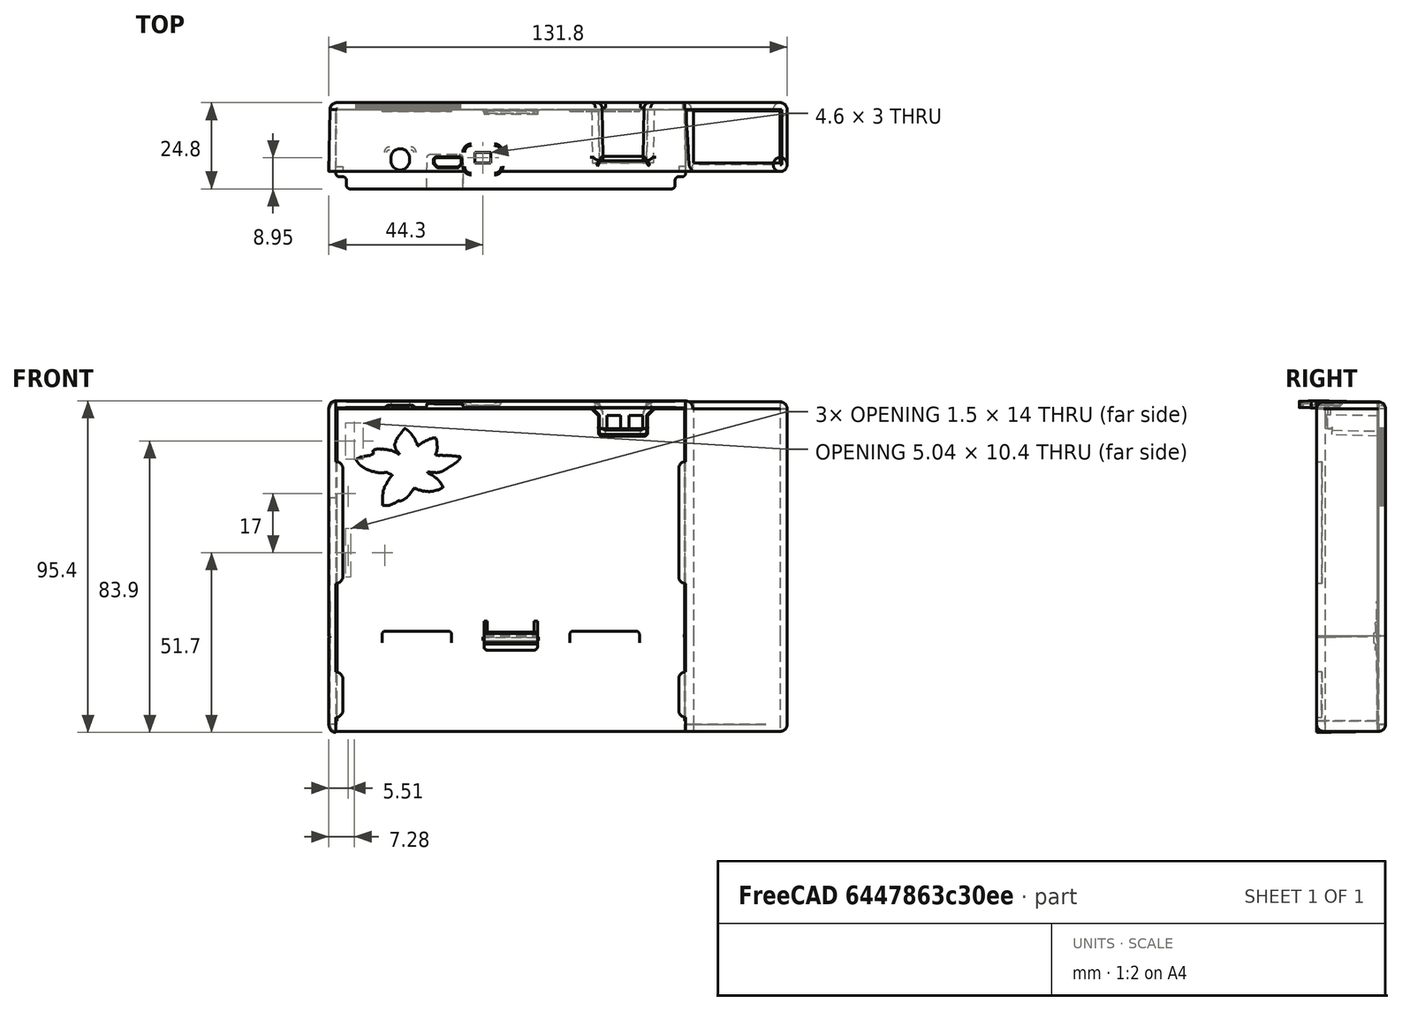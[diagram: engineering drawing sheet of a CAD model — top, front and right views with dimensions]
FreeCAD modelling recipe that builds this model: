
FCSTD DOCUMENT  (FreeCAD 0.20R29410 (Git))
Label: N2CaseOnePeice_10_18_2022
License: All rights reserved
LicenseURL: http://en.wikipedia.org/wiki/All_rights_reserved
objects: Part::Box×22, Part::Cylinder×12, Part::MultiFuse×9, Part::Cut×9, Part::Sphere×4, Part::Feature×3, Mesh::Feature×1
note: 59 computed .brp shape members not serialized (recipe doc carries the construction recipe); baked Part::Feature solids carry a one-line shape summary decoded from their .brp

FEATURE [Part::Feature] Solid  label="N2_BOTTOM_COVER"
  shape: bbox 104.6 x 25.21 x 71.78 mm, 343 faces (baked)
FEATURE [Part::Feature] Solid001  label="N2_TOP_COVER"
  shape: bbox 104.6 x 24.81 x 29.22 mm, 349 faces (baked)
FEATURE [Part::Box] Box  label="Cube"
  AttacherType = Attacher::AttachEngine3D
  Height = 15
  Length = 62.5
  Placement = pos=(-49,18,44) rot=(0,1,0;1.5708rad)
  Width = 2
FEATURE [Part::MultiFuse] Fusion  label="BottomCover"
  Shapes = -> [Solid,Box]
FEATURE [Part::Box] Box001  label="Cube001"
  AttacherType = Attacher::AttachEngine3D
  Height = 15
  Length = 97.5
  Placement = pos=(48.5,20,-3.5) rot=(0,1,0;3.14159rad)
  Width = 2
FEATURE [Part::Cut] Cut
  Base = -> Fusion
  Tool = -> Box001
FEATURE [Part::Box] Box002  label="usbEthernet"
  AttacherType = Attacher::AttachEngine3D
  Height = 25
  Length = 72
  Placement = pos=(52.5,2.6,47.4) rot=(0,1,0;1.5708rad)
  Width = 15
FEATURE [Part::Box] Box003  label="usbEthernetCover"
  AttacherType = Attacher::AttachEngine3D
  Height = 27.5
  Length = 72
  Placement = pos=(50.5,2.2,47.4) rot=(0,1,0;1.5708rad)
  Width = 15.85
FEATURE [Part::Box] Box004  label="usbEthernetCover001"
  AttacherType = Attacher::AttachEngine3D
  Height = 27.52
  Length = 65.19
  Placement = pos=(49.98,17.6,45.39) rot=(0,1,0;1.5708rad)
  Width = 2.4
FEATURE [Part::Box] Box005  label="usbEthernetCover002"
  AttacherType = Attacher::AttachEngine3D
  Height = 2
  Length = 65.19
  Placement = pos=(77.5,2.2,45.39) rot=(0,1,0;1.5708rad)
  Width = 15.8
FEATURE [Part::Cylinder] Cylinder
  Angle = 90
  AttacherType = Attacher::AttachEngine3D
  FirstAngle = 0
  Height = 65.2
  Placement = pos=(77.5,2.2,-19.8) rot=(0,0,-1;1.5708rad)
  Radius = 2
  SecondAngle = 0
FEATURE [Part::Cylinder] Cylinder001
  Angle = 90
  AttacherType = Attacher::AttachEngine3D
  FirstAngle = 0
  Height = 27.5
  Placement = pos=(77.5,18,45.4) rot=(0,-1,0;1.5708rad)
  Radius = 2
  SecondAngle = 0
FEATURE [Part::Cylinder] Cylinder002
  Angle = 90
  AttacherType = Attacher::AttachEngine3D
  FirstAngle = 0
  Height = 15.8
  Placement = pos=(77.5,2.2,45.4) rot=(0.57735,0.57735,0.57735;4.18879rad)
  Radius = 2
  SecondAngle = 0
FEATURE [Part::Cylinder] Cylinder003
  Angle = 90
  AttacherType = Attacher::AttachEngine3D
  FirstAngle = 0
  Height = 65.2
  Placement = pos=(77.5,18,-19.8) rot=(0,0,1;0rad)
  Radius = 2
  SecondAngle = 0
FEATURE [Part::Box] Box006  label="usbEthernetCover003"
  AttacherType = Attacher::AttachEngine3D
  Height = 27.2
  Length = 65.19
  Placement = pos=(50.3,0.2,45.39) rot=(0,1,0;1.5708rad)
  Width = 2.4
FEATURE [Part::Cylinder] Cylinder004
  Angle = 90
  AttacherType = Attacher::AttachEngine3D
  FirstAngle = 0
  Height = 26.4
  Placement = pos=(77.5,2.2,45.4) rot=(0.57735,-0.57735,-0.57735;2.0944rad)
  Radius = 2
  SecondAngle = 0
FEATURE [Part::Sphere] Sphere
  Angle1 = -90
  Angle2 = 90
  Angle3 = 360
  AttacherType = Attacher::AttachEngine3D
  Placement = pos=(77.5,18,45.4) rot=(0,0,1;0rad)
  Radius = 2
FEATURE [Part::Sphere] Sphere001
  Angle1 = -90
  Angle2 = 90
  Angle3 = 360
  AttacherType = Attacher::AttachEngine3D
  Placement = pos=(77.5,2.2,45.4) rot=(0,0,1;0rad)
  Radius = 2
FEATURE [Part::MultiFuse] Fusion001  label="usbCover"
  Shapes = -> [Box003,Box004,Box005,Cylinder,Cylinder001,Cylinder002,Cylinder003,Box006,Cylinder004,Sphere,Sphere001]
FEATURE [Part::MultiFuse] Fusion002
  Shapes = -> [Cut,Fusion001]
FEATURE [Part::Cut] Cut001  label="front"
  Base = -> Fusion002
  Tool = -> Box002
FEATURE [Part::Box] Box007  label="Cube002"
  AttacherType = Attacher::AttachEngine3D
  Height = 10
  Length = 30
  Placement = pos=(79.5,0,-19.8) rot=(0,1,0;3.14159rad)
  Width = 20
FEATURE [Part::Cut] Cut002
  Base = -> Cut001
  Tool = -> Box007
FEATURE [Part::Box] Box008  label="Cube003"
  AttacherType = Attacher::AttachEngine3D
  Height = 10
  Length = 30
  Placement = pos=(79.5,0,-19.8) rot=(0,1,0;3.14159rad)
  Width = 20
FEATURE [Part::Cut] Cut003  label="front001"
  Base = -> Cut002
  Tool = -> Box008
FEATURE [Part::Box] Box009  label="usbEthernet001"
  AttacherType = Attacher::AttachEngine3D
  Height = 25
  Length = 72
  Placement = pos=(52.5,2.6,6.3) rot=(0,1,0;1.5708rad)
  Width = 15
FEATURE [Part::Box] Box010  label="usbEthernetCover004"
  AttacherType = Attacher::AttachEngine3D
  Height = 27.5
  Length = 72
  Placement = pos=(50.5,2.2,-19.8) rot=(0,1,0;1.5708rad)
  Width = 15.85
FEATURE [Part::Box] Box011  label="usbEthernetCover005"
  AttacherType = Attacher::AttachEngine3D
  Height = 27.52
  Length = 65.19
  Placement = pos=(49.98,17.6,-19.8) rot=(0,1,0;1.5708rad)
  Width = 2.4
FEATURE [Part::Box] Box012  label="usbEthernetCover006"
  AttacherType = Attacher::AttachEngine3D
  Height = 2
  Length = 65.19
  Placement = pos=(77.5,2.2,-19.8) rot=(0,1,0;1.5708rad)
  Width = 15.8
FEATURE [Part::Box] Box013  label="usbEthernetCover007"
  AttacherType = Attacher::AttachEngine3D
  Height = 27.2
  Length = 65.19
  Placement = pos=(50.3,0.2,-19.8) rot=(0,1,0;1.5708rad)
  Width = 2.4
FEATURE [Part::Box] Box016  label="Cube005"
  AttacherType = Attacher::AttachEngine3D
  Height = 50
  Length = 29.5
  Placement = pos=(79.5,0,-45.4) rot=(0,1,0;3.14159rad)
  Width = 20
FEATURE [Part::MultiFuse] Fusion003
  Shapes = -> [Solid001,Box010,Box011,Box012,Box013]
FEATURE [Part::Cut] Cut004
  Base = -> Fusion003
  Tool = -> Box016
FEATURE [Part::Cut] Cut005
  Base = -> Cut004
  Tool = -> Box009
FEATURE [Part::Box] Box017  label="Cube006"
  AttacherType = Attacher::AttachEngine3D
  Height = 50
  Length = 23.5
  Placement = pos=(73.4,17.6,-45.39) rot=(0,1,0;3.14159rad)
  Width = 20
FEATURE [Part::Cut] Cut006
  Base = -> Cut005
  Tool = -> Box017
FEATURE [Part::Cylinder] Cylinder005
  Angle = 90
  AttacherType = Attacher::AttachEngine3D
  FirstAngle = 0
  Height = 65.2
  Placement = pos=(77.5,2.2,-45.4) rot=(0,0,-1;1.5708rad)
  Radius = 2
  SecondAngle = 0
FEATURE [Part::Cylinder] Cylinder006
  Angle = 90
  AttacherType = Attacher::AttachEngine3D
  FirstAngle = 0
  Height = 27.5
  Placement = pos=(77.5,18,-45.4) rot=(0,-1,0;1.5708rad)
  Radius = 2
  SecondAngle = 0
FEATURE [Part::Cylinder] Cylinder007
  Angle = 90
  AttacherType = Attacher::AttachEngine3D
  FirstAngle = 0
  Height = 15.8
  Placement = pos=(77.5,2.2,-45.4) rot=(-1,0,0;1.5708rad)
  Radius = 2
  SecondAngle = 0
FEATURE [Part::Cylinder] Cylinder008
  Angle = 90
  AttacherType = Attacher::AttachEngine3D
  FirstAngle = 0
  Height = 65.2
  Placement = pos=(77.5,18,-45.4) rot=(0,0,1;0rad)
  Radius = 2
  SecondAngle = 0
FEATURE [Part::Cylinder] Cylinder009
  Angle = 90
  AttacherType = Attacher::AttachEngine3D
  FirstAngle = 0
  Height = 27.6
  Placement = pos=(77.5,2.2,-45.4) rot=(0.707107,0,-0.707107;3.14159rad)
  Radius = 2
  SecondAngle = 0
FEATURE [Part::Cylinder] Cylinder010
  Angle = 90
  AttacherType = Attacher::AttachEngine3D
  FirstAngle = 0
  Height = 27.6
  Placement = pos=(77.5,18,-45.4) rot=(0.57735,0.57735,-0.57735;4.18879rad)
  Radius = 2
  SecondAngle = 0
FEATURE [Part::Box] Box018  label="Cube007"
  AttacherType = Attacher::AttachEngine3D
  Height = 2
  Length = 27.6
  Placement = pos=(49.9,18,-45.4) rot=(1,0,0;3.14159rad)
  Width = 15.8
FEATURE [Part::Box] Box019  label="usbEthernet002"
  AttacherType = Attacher::AttachEngine3D
  Height = 25
  Length = 72
  Placement = pos=(52.5,2.6,-2.5) rot=(0,1,0;1.5708rad)
  Width = 15
FEATURE [Part::Sphere] Sphere002
  Angle1 = -90
  Angle2 = 90
  Angle3 = 360
  AttacherType = Attacher::AttachEngine3D
  Placement = pos=(77.5,18,-45.4) rot=(0,0,1;0rad)
  Radius = 2
FEATURE [Part::Sphere] Sphere003
  Angle1 = -90
  Angle2 = 90
  Angle3 = 360
  AttacherType = Attacher::AttachEngine3D
  Placement = pos=(77.5,2.2,-45.4) rot=(0,0,1;0rad)
  Radius = 2
FEATURE [Part::Box] Box020  label="Cube008"
  AttacherType = Attacher::AttachEngine3D
  Height = 40
  Length = 10
  Placement = pos=(73.6,0,-19.8) rot=(0,0,1;0rad)
  Width = 22
FEATURE [Part::MultiFuse] Fusion004  label="cuts"
  Shapes = -> [Box020,Box019]
FEATURE [Part::MultiFuse] Fusion005
  Shapes = -> [Sphere003,Cut006,Cylinder005,Cylinder006,Cylinder007,Cylinder008,Cylinder009,Cylinder010,Box018,Sphere002]
FEATURE [Part::Cut] Cut007  label="back"
  Base = -> Fusion005
  Tool = -> Fusion004
FEATURE [Part::Box] Box021  label="Cube009"
  AttacherType = Attacher::AttachEngine3D
  Height = 32.5
  Length = 97.5
  Placement = pos=(48.5,18,-11.9) rot=(0,1,0;3.14159rad)
  Width = 2
FEATURE [Part::MultiFuse] Fusion006  label="back001"
  Shapes = -> [Cut007,Box021]
FEATURE [Part::Cylinder] Cylinder011
  Angle = 90
  AttacherType = Attacher::AttachEngine3D
  FirstAngle = 0
  Height = 65.2
  Placement = pos=(-50,18,-45.4) rot=(0,0,1;1.5708rad)
  Radius = 2
  SecondAngle = 0
FEATURE [Part::Box] Box070  label="Cube010"
  AttacherType = Attacher::AttachEngine3D
  Height = 20
  Length = 1.7
  Placement = pos=(-50.3,0.2,-10) rot=(0,1,0;3.14159rad)
  Width = 17.8
FEATURE [Part::Box] Box071  label="cuts001"
  AttacherType = Attacher::AttachEngine3D
  Height = 10
  Length = 23
  Placement = pos=(50.3,-5,-54.4) rot=(0,0,1;1.5708rad)
  Width = 100.6
FEATURE [Part::Feature] logo3mmWidth001_solid001  label="logo3mmWidth001 (Solid)001"
  Placement = pos=(-47.5,15.27,43.04) rot=(-1,0,0;1.5708rad)
  shape: bbox 30 x 4.944 x 22.21 mm, 7244 faces (baked)
FEATURE [Part::MultiFuse] Fusion007
  Shapes = -> [Cut003,Fusion006,Cylinder011,Box070]
FEATURE [Part::MultiFuse] Fusion008
  Shapes = -> [logo3mmWidth001_solid001,Box071]
FEATURE [Part::Cut] Cut008  label="n2Case"
  Base = -> Fusion007
  Tool = -> Fusion008
FEATURE [Mesh::Feature] _9G1ElevatedDesign  label="99G1ElevatedDesign"
  Placement = pos=(-31.68,17.29,30.95) rot=(1,0,0;4.71239rad)
